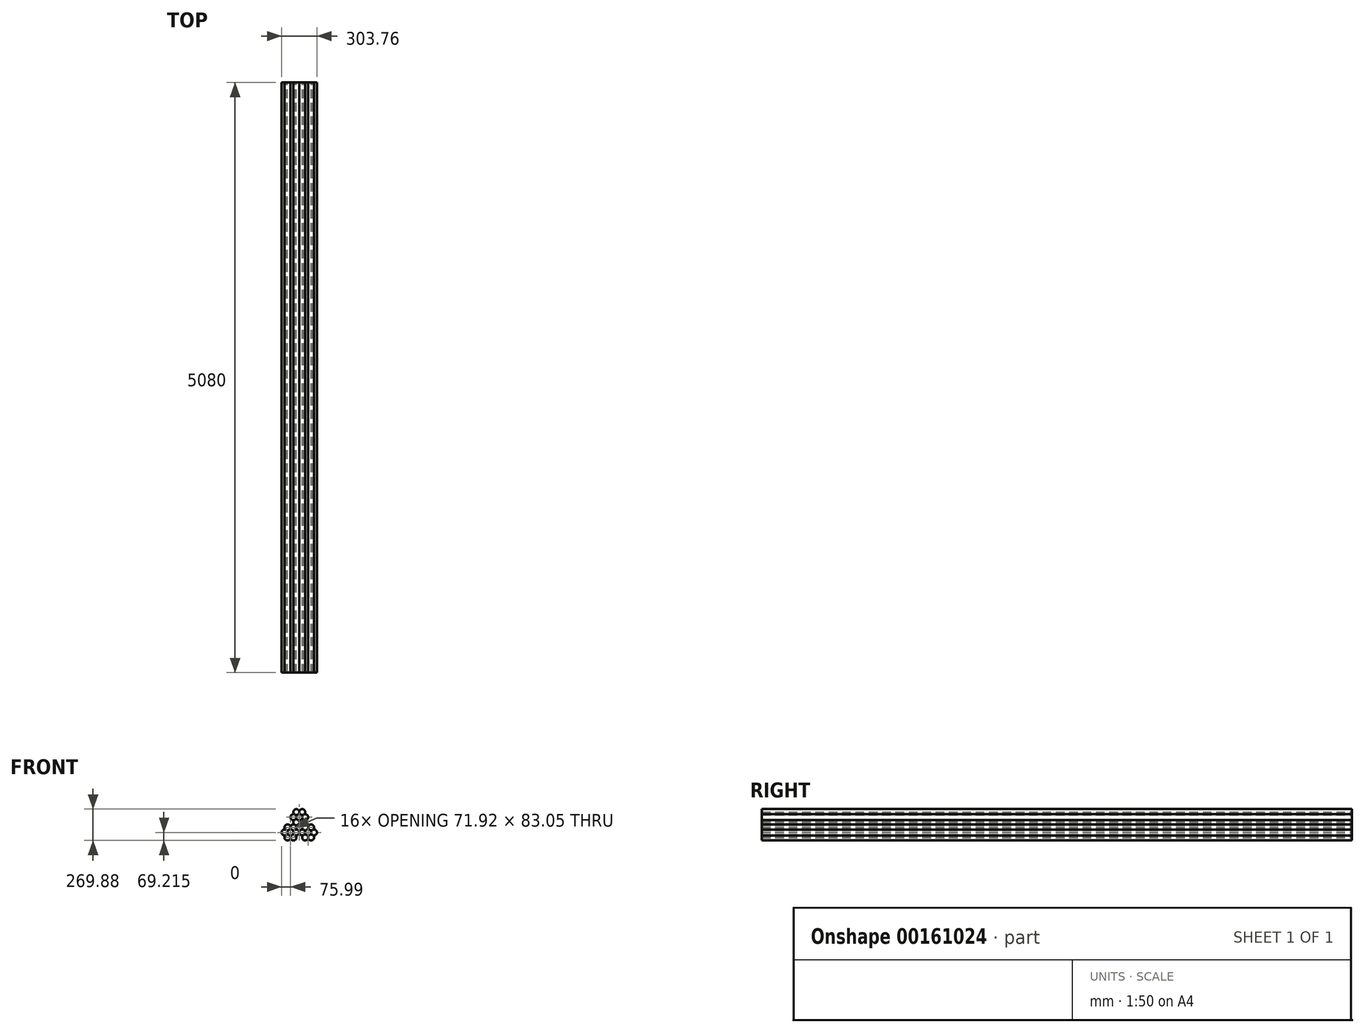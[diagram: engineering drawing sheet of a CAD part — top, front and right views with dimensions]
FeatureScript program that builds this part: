
annotation { "Feature Type Name" : "Feature", "Feature Type Description" : "" }
export const myFeature = defineFeature(function(context is Context, id is Id, definition is map)
    precondition{}
    {
        {
            var Q0;
            Q0=qCreatedBy(makeId("Front.planeOp"),FACE);
            var sketch = newSketch(context, id + "F0", { "sketchPlane" : qUnion([Q0])});
            skCircle(sketch, "E0.cCircle", {"center": v(0, 0) * mm, "radius": 43.82 * mm, "construction": true});
            skLineSegment(sketch, "E0.0", {"start": v(25.3, 43.81) * mm, "end": v(50.6, 0) * mm, "construction": true});
            skLineSegment(sketch, "E0.1", {"start": v(50.6, 0) * mm, "end": v(25.3, -43.82) * mm, "construction": true});
            skLineSegment(sketch, "E0.2", {"start": v(25.3, -43.82) * mm, "end": v(-25.3, -43.82) * mm, "construction": true});
            skLineSegment(sketch, "E0.3", {"start": v(-25.3, -43.82) * mm, "end": v(-50.6, 0) * mm, "construction": true});
            skLineSegment(sketch, "E0.4", {"start": v(-50.6, 0) * mm, "end": v(-25.3, 43.82) * mm, "construction": true});
            skLineSegment(sketch, "E0.5", {"start": v(-25.3, 43.82) * mm, "end": v(25.3, 43.82) * mm, "construction": true});
            skPoint(sketch, "E0.0.midPoint", {"position": v(37.94, 21.9) * mm});
            skCircle(sketch, "E1.cCircle", {"center": v(0, 87.63) * mm, "radius": 43.82 * mm, "construction": true});
            skLineSegment(sketch, "E1.0", {"start": v(25.3, 43.82) * mm, "end": v(-25.3, 43.82) * mm, "construction": true});
            skLineSegment(sketch, "E1.1", {"start": v(-25.3, 43.82) * mm, "end": v(-50.6, 87.63) * mm, "construction": true});
            skLineSegment(sketch, "E1.2", {"start": v(-50.6, 87.63) * mm, "end": v(-25.3, 131.45) * mm, "construction": true});
            skLineSegment(sketch, "E1.3", {"start": v(-25.3, 131.45) * mm, "end": v(25.3, 131.45) * mm, "construction": true});
            skLineSegment(sketch, "E1.4", {"start": v(25.3, 131.45) * mm, "end": v(50.6, 87.63) * mm, "construction": true});
            skLineSegment(sketch, "E1.5", {"start": v(50.6, 87.63) * mm, "end": v(25.3, 43.82) * mm, "construction": true});
            skPoint(sketch, "E1.0.midPoint", {"position": v(0, 43.82) * mm});
            skCircle(sketch, "E2.cCircle", {"center": v(75.89, -43.81) * mm, "radius": 43.81 * mm, "construction": true});
            skLineSegment(sketch, "E2.0", {"start": v(25.3, -43.81) * mm, "end": v(50.6, 0) * mm, "construction": true});
            skLineSegment(sketch, "E2.1", {"start": v(50.6, 0) * mm, "end": v(101.19, 0) * mm, "construction": true});
            skLineSegment(sketch, "E2.2", {"start": v(101.19, 0) * mm, "end": v(126.48, -43.81) * mm, "construction": true});
            skLineSegment(sketch, "E2.3", {"start": v(126.48, -43.81) * mm, "end": v(101.19, -87.63) * mm, "construction": true});
            skLineSegment(sketch, "E2.4", {"start": v(101.19, -87.63) * mm, "end": v(50.6, -87.63) * mm, "construction": true});
            skLineSegment(sketch, "E2.5", {"start": v(50.6, -87.63) * mm, "end": v(25.3, -43.81) * mm, "construction": true});
            skPoint(sketch, "E2.0.midPoint", {"position": v(37.94, -21.9) * mm});
            skCircle(sketch, "E3.cCircle", {"center": v(-75.89, -43.81) * mm, "radius": 43.81 * mm, "construction": true});
            skLineSegment(sketch, "E3.0", {"start": v(-50.6, 0) * mm, "end": v(-25.3, -43.81) * mm, "construction": true});
            skLineSegment(sketch, "E3.1", {"start": v(-25.3, -43.81) * mm, "end": v(-50.6, -87.63) * mm, "construction": true});
            skLineSegment(sketch, "E3.2", {"start": v(-50.6, -87.63) * mm, "end": v(-101.19, -87.63) * mm, "construction": true});
            skLineSegment(sketch, "E3.3", {"start": v(-101.19, -87.63) * mm, "end": v(-126.48, -43.81) * mm, "construction": true});
            skLineSegment(sketch, "E3.4", {"start": v(-126.48, -43.81) * mm, "end": v(-101.19, 0) * mm, "construction": true});
            skLineSegment(sketch, "E3.5", {"start": v(-101.19, 0) * mm, "end": v(-50.6, 0) * mm, "construction": true});
            skPoint(sketch, "E3.0.midPoint", {"position": v(-36.58, -24.28) * mm});
            skArc(sketch, "E4", {"start": v(0, 129.16) * mm, "mid": v(12.6, 109.45) * mm, "end": v(35.96, 108.4) * mm});
            skArc(sketch, "E5", {"start": v(35.96, 108.4) * mm, "mid": v(25.2, 87.63) * mm, "end": v(35.96, 66.87) * mm});
            skArc(sketch, "E6", {"start": v(35.96, 66.87) * mm, "mid": v(12.6, 65.81) * mm, "end": v(0, 46.1) * mm});
            skArc(sketch, "E7", {"start": v(37.9, 22) * mm, "mid": v(37.9, 22) * mm, "end": v(37.9, 22) * mm});
            skArc(sketch, "E8", {"start": v(75.79, 0) * mm, "mid": v(75.79, 0) * mm, "end": v(75.79, 0) * mm});
            skArc(sketch, "E9", {"start": v(113.78, -21.82) * mm, "mid": v(113.78, -21.82) * mm, "end": v(113.78, -21.82) * mm});
            skArc(sketch, "E10", {"start": v(39.93, -64.58) * mm, "mid": v(50.7, -43.81) * mm, "end": v(39.93, -23.05) * mm});
            skArc(sketch, "E11", {"start": v(0.1, 43.81) * mm, "mid": v(0.1, 43.82) * mm, "end": v(0.1, 43.82) * mm});
            skArc(sketch, "E12", {"start": v(-35.96, 66.87) * mm, "mid": v(-25.2, 87.63) * mm, "end": v(-35.96, 108.4) * mm});
            skArc(sketch, "E13", {"start": v(0.1, 131.44) * mm, "mid": v(0.1, 131.44) * mm, "end": v(0.1, 131.45) * mm});
            skArc(sketch, "E14", {"start": v(-37.9, -22) * mm, "mid": v(-37.9, -22) * mm, "end": v(-37.9, -22) * mm});
            skArc(sketch, "E15", {"start": v(0.1, -43.81) * mm, "mid": v(0.1, -43.81) * mm, "end": v(0.1, -43.81) * mm});
            skArc(sketch, "E16", {"start": v(-111.85, -23.05) * mm, "mid": v(-88.49, -22) * mm, "end": v(-75.89, -2.29) * mm});
            skArc(sketch, "E17", {"start": v(-113.78, -21.82) * mm, "mid": v(-113.78, -21.82) * mm, "end": v(-113.78, -21.82) * mm});
            skArc(sketch, "E18", {"start": v(-75.79, -87.63) * mm, "mid": v(-75.79, -87.63) * mm, "end": v(-75.79, -87.63) * mm});
            skArc(sketch, "E19", {"start": v(-37.9, -65.63) * mm, "mid": v(-37.9, -65.63) * mm, "end": v(-37.9, -65.63) * mm});
            skArc(sketch, "E20", {"start": v(76, -87.63) * mm, "mid": v(76, -87.63) * mm, "end": v(76, -87.63) * mm});
            skArc(sketch, "E21", {"start": v(113.89, -65.63) * mm, "mid": v(113.89, -65.63) * mm, "end": v(113.89, -65.63) * mm});
            skArc(sketch, "E22.trimOffspring", {"start": v(0, 133.73) * mm, "mid": v(-38, 153.44) * mm, "end": v(-39.93, 110.68) * mm});
            skArc(sketch, "E23.trimOffspring", {"start": v(-0.1, 131.45) * mm, "mid": v(-0.1, 131.44) * mm, "end": v(-0.1, 131.44) * mm});
            skArc(sketch, "E24.trimOffspring", {"start": v(39.93, 110.68) * mm, "mid": v(38, 153.44) * mm, "end": v(0, 133.73) * mm});
            skArc(sketch, "E25.trimOffspring", {"start": v(38, 109.45) * mm, "mid": v(38, 109.45) * mm, "end": v(38, 109.45) * mm});
            skArc(sketch, "E26.trimOffspring", {"start": v(37.9, 65.63) * mm, "mid": v(37.9, 65.63) * mm, "end": v(37.9, 65.63) * mm});
            skArc(sketch, "E27.trimOffspring", {"start": v(38, 65.81) * mm, "mid": v(38, 65.81) * mm, "end": v(38, 65.81) * mm});
            skArc(sketch, "E28.trimOffspring", {"start": v(39.93, 64.58) * mm, "mid": v(76, 87.63) * mm, "end": v(39.93, 110.68) * mm});
            skArc(sketch, "E29.trimOffspring", {"start": v(0, 41.53) * mm, "mid": v(12.6, 21.82) * mm, "end": v(35.96, 20.76) * mm});
            skArc(sketch, "E30.trimOffspring", {"start": v(0, 46.1) * mm, "mid": v(-12.6, 65.81) * mm, "end": v(-35.96, 66.87) * mm});
            skArc(sketch, "E31.trimOffspring", {"start": v(-0.1, 43.82) * mm, "mid": v(-0.1, 43.82) * mm, "end": v(-0.1, 43.81) * mm});
            skArc(sketch, "E32.trimOffspring", {"start": v(-38, 65.81) * mm, "mid": v(-38, 65.81) * mm, "end": v(-38, 65.81) * mm});
            skArc(sketch, "E33.trimOffspring", {"start": v(-39.93, 64.58) * mm, "mid": v(-50.7, 43.82) * mm, "end": v(-39.93, 23.05) * mm});
            skArc(sketch, "E34.trimOffspring", {"start": v(-37.9, 65.63) * mm, "mid": v(-37.9, 65.63) * mm, "end": v(-37.9, 65.63) * mm});
            skArc(sketch, "E35.trimOffspring", {"start": v(-37.9, 109.63) * mm, "mid": v(-37.9, 109.63) * mm, "end": v(-37.9, 109.63) * mm});
            skArc(sketch, "E36.trimOffspring", {"start": v(-35.96, 108.4) * mm, "mid": v(-12.6, 109.45) * mm, "end": v(0, 129.16) * mm});
            skArc(sketch, "E37.trimOffspring", {"start": v(-38, 109.45) * mm, "mid": v(-38, 109.45) * mm, "end": v(-38, 109.45) * mm});
            skArc(sketch, "E38.trimOffspring", {"start": v(-39.93, 110.68) * mm, "mid": v(-76, 87.63) * mm, "end": v(-39.93, 64.58) * mm});
            skArc(sketch, "E39.trimOffspring", {"start": v(39.93, 23.05) * mm, "mid": v(50.7, 43.81) * mm, "end": v(39.93, 64.58) * mm});
            skArc(sketch, "E40.trimOffspring", {"start": v(38, 21.82) * mm, "mid": v(38, 21.82) * mm, "end": v(38, 21.82) * mm});
            skArc(sketch, "E41.trimOffspring", {"start": v(35.96, 20.76) * mm, "mid": v(25.2, 0) * mm, "end": v(35.96, -20.76) * mm});
            skArc(sketch, "E42.trimOffspring", {"start": v(75.89, 2.29) * mm, "mid": v(63.3, 22) * mm, "end": v(39.93, 23.05) * mm});
            skArc(sketch, "E43.trimOffspring", {"start": v(76, 0) * mm, "mid": v(76, 0) * mm, "end": v(76, 0) * mm});
            skArc(sketch, "E44.trimOffspring", {"start": v(75.89, -2.29) * mm, "mid": v(88.49, -22) * mm, "end": v(111.85, -23.05) * mm});
            skArc(sketch, "E45.trimOffspring", {"start": v(115.82, -20.76) * mm, "mid": v(113.89, 22) * mm, "end": v(75.89, 2.29) * mm});
            skArc(sketch, "E46.trimOffspring", {"start": v(111.85, -23.05) * mm, "mid": v(101.08, -43.81) * mm, "end": v(111.85, -64.58) * mm});
            skArc(sketch, "E47.trimOffspring", {"start": v(113.89, -22) * mm, "mid": v(113.89, -22) * mm, "end": v(113.89, -22) * mm});
            skArc(sketch, "E48.trimOffspring", {"start": v(115.82, -66.87) * mm, "mid": v(151.88, -43.81) * mm, "end": v(115.82, -20.76) * mm});
            skArc(sketch, "E49.trimOffspring", {"start": v(113.78, -65.81) * mm, "mid": v(113.78, -65.81) * mm, "end": v(113.78, -65.81) * mm});
            skArc(sketch, "E50.trimOffspring", {"start": v(111.85, -64.58) * mm, "mid": v(88.49, -65.63) * mm, "end": v(75.89, -85.34) * mm});
            skArc(sketch, "E51.trimOffspring", {"start": v(75.89, -89.92) * mm, "mid": v(113.89, -109.63) * mm, "end": v(115.82, -66.87) * mm});
            skArc(sketch, "E52.trimOffspring", {"start": v(75.89, -85.34) * mm, "mid": v(63.3, -65.63) * mm, "end": v(39.93, -64.58) * mm});
            skArc(sketch, "E53.trimOffspring", {"start": v(75.79, -87.63) * mm, "mid": v(75.79, -87.63) * mm, "end": v(75.79, -87.63) * mm});
            skArc(sketch, "E54.trimOffspring", {"start": v(37.9, -65.63) * mm, "mid": v(37.9, -65.63) * mm, "end": v(37.9, -65.63) * mm});
            skArc(sketch, "E55.trimOffspring", {"start": v(38, -65.81) * mm, "mid": v(38, -65.81) * mm, "end": v(38, -65.81) * mm});
            skArc(sketch, "E56.trimOffspring", {"start": v(35.96, -66.87) * mm, "mid": v(37.9, -109.63) * mm, "end": v(75.89, -89.92) * mm});
            skArc(sketch, "E57.trimOffspring", {"start": v(38, -21.82) * mm, "mid": v(38, -21.82) * mm, "end": v(38, -21.82) * mm});
            skArc(sketch, "E58.trimOffspring", {"start": v(39.93, -23.05) * mm, "mid": v(63.3, -22) * mm, "end": v(75.89, -2.29) * mm});
            skArc(sketch, "E59.trimOffspring", {"start": v(37.9, -22) * mm, "mid": v(37.9, -22) * mm, "end": v(37.9, -22) * mm});
            skArc(sketch, "E60.trimOffspring", {"start": v(35.96, -20.76) * mm, "mid": v(12.6, -21.82) * mm, "end": v(0, -41.53) * mm});
            skArc(sketch, "E61.trimOffspring", {"start": v(0, -46.1) * mm, "mid": v(12.6, -65.81) * mm, "end": v(35.96, -66.87) * mm});
            skArc(sketch, "E62.trimOffspring", {"start": v(0, -41.53) * mm, "mid": v(-12.6, -21.82) * mm, "end": v(-35.96, -20.76) * mm});
            skArc(sketch, "E63.trimOffspring", {"start": v(-0.1, -43.81) * mm, "mid": v(-0.1, -43.81) * mm, "end": v(-0.1, -43.82) * mm});
            skArc(sketch, "E64.trimOffspring", {"start": v(-39.93, -23.05) * mm, "mid": v(-50.7, -43.81) * mm, "end": v(-39.93, -64.58) * mm});
            skArc(sketch, "E65.trimOffspring", {"start": v(-35.96, -20.76) * mm, "mid": v(-25.2, 0) * mm, "end": v(-35.96, 20.76) * mm});
            skArc(sketch, "E66.trimOffspring", {"start": v(-38, -21.82) * mm, "mid": v(-38, -21.82) * mm, "end": v(-38, -21.82) * mm});
            skArc(sketch, "E67.trimOffspring", {"start": v(-39.93, 23.05) * mm, "mid": v(-63.3, 22) * mm, "end": v(-75.89, 2.29) * mm});
            skArc(sketch, "E68.trimOffspring", {"start": v(-38, 21.82) * mm, "mid": v(-38, 21.82) * mm, "end": v(-38, 21.82) * mm});
            skArc(sketch, "E69.trimOffspring", {"start": v(-37.9, 22) * mm, "mid": v(-37.9, 22) * mm, "end": v(-37.9, 22) * mm});
            skArc(sketch, "E70.trimOffspring", {"start": v(-35.96, 20.76) * mm, "mid": v(-12.6, 21.82) * mm, "end": v(0, 41.53) * mm});
            skArc(sketch, "E71.trimOffspring", {"start": v(-113.89, -22) * mm, "mid": v(-113.89, -22) * mm, "end": v(-113.89, -22) * mm});
            skArc(sketch, "E72.trimOffspring", {"start": v(-115.82, -20.76) * mm, "mid": v(-151.88, -43.81) * mm, "end": v(-115.82, -66.87) * mm});
            skArc(sketch, "E73.trimOffspring", {"start": v(-75.89, 2.29) * mm, "mid": v(-113.89, 22) * mm, "end": v(-115.82, -20.76) * mm});
            skArc(sketch, "E74.trimOffspring", {"start": v(-76, 0) * mm, "mid": v(-76, 0) * mm, "end": v(-76, 0) * mm});
            skArc(sketch, "E75.trimOffspring", {"start": v(-75.79, 0) * mm, "mid": v(-75.79, 0) * mm, "end": v(-75.79, 0) * mm});
            skArc(sketch, "E76.trimOffspring", {"start": v(-75.89, -2.29) * mm, "mid": v(-63.3, -22) * mm, "end": v(-39.93, -23.05) * mm});
            skArc(sketch, "E77.trimOffspring", {"start": v(-35.96, -66.87) * mm, "mid": v(-12.6, -65.81) * mm, "end": v(0, -46.1) * mm});
            skArc(sketch, "E78.trimOffspring", {"start": v(-39.93, -64.58) * mm, "mid": v(-63.3, -65.63) * mm, "end": v(-75.89, -85.34) * mm});
            skArc(sketch, "E79.trimOffspring", {"start": v(-38, -65.81) * mm, "mid": v(-38, -65.81) * mm, "end": v(-38, -65.81) * mm});
            skArc(sketch, "E80.trimOffspring", {"start": v(-75.89, -89.92) * mm, "mid": v(-37.9, -109.63) * mm, "end": v(-35.96, -66.87) * mm});
            skArc(sketch, "E81.trimOffspring", {"start": v(-75.89, -85.34) * mm, "mid": v(-88.49, -65.63) * mm, "end": v(-111.85, -64.58) * mm});
            skArc(sketch, "E82.trimOffspring", {"start": v(-76, -87.63) * mm, "mid": v(-76, -87.63) * mm, "end": v(-76, -87.63) * mm});
            skArc(sketch, "E83.trimOffspring", {"start": v(-115.82, -66.87) * mm, "mid": v(-113.89, -109.63) * mm, "end": v(-75.89, -89.92) * mm});
            skArc(sketch, "E84.trimOffspring", {"start": v(-113.78, -65.81) * mm, "mid": v(-113.78, -65.81) * mm, "end": v(-113.78, -65.81) * mm});
            skArc(sketch, "E85.trimOffspring", {"start": v(-111.85, -64.58) * mm, "mid": v(-101.08, -43.81) * mm, "end": v(-111.85, -23.05) * mm});
            skArc(sketch, "E86.trimOffspring", {"start": v(-113.89, -65.63) * mm, "mid": v(-113.89, -65.63) * mm, "end": v(-113.89, -65.63) * mm});
            skSolve(sketch);
        }
        {
            var Q0;
            Q0 = qSketchRegion(id + "F0", true);
            extrude(context, id + "F1", {"entities" : qUnion([Q0]), "depth" : 5080 * mm});
        }
    });
